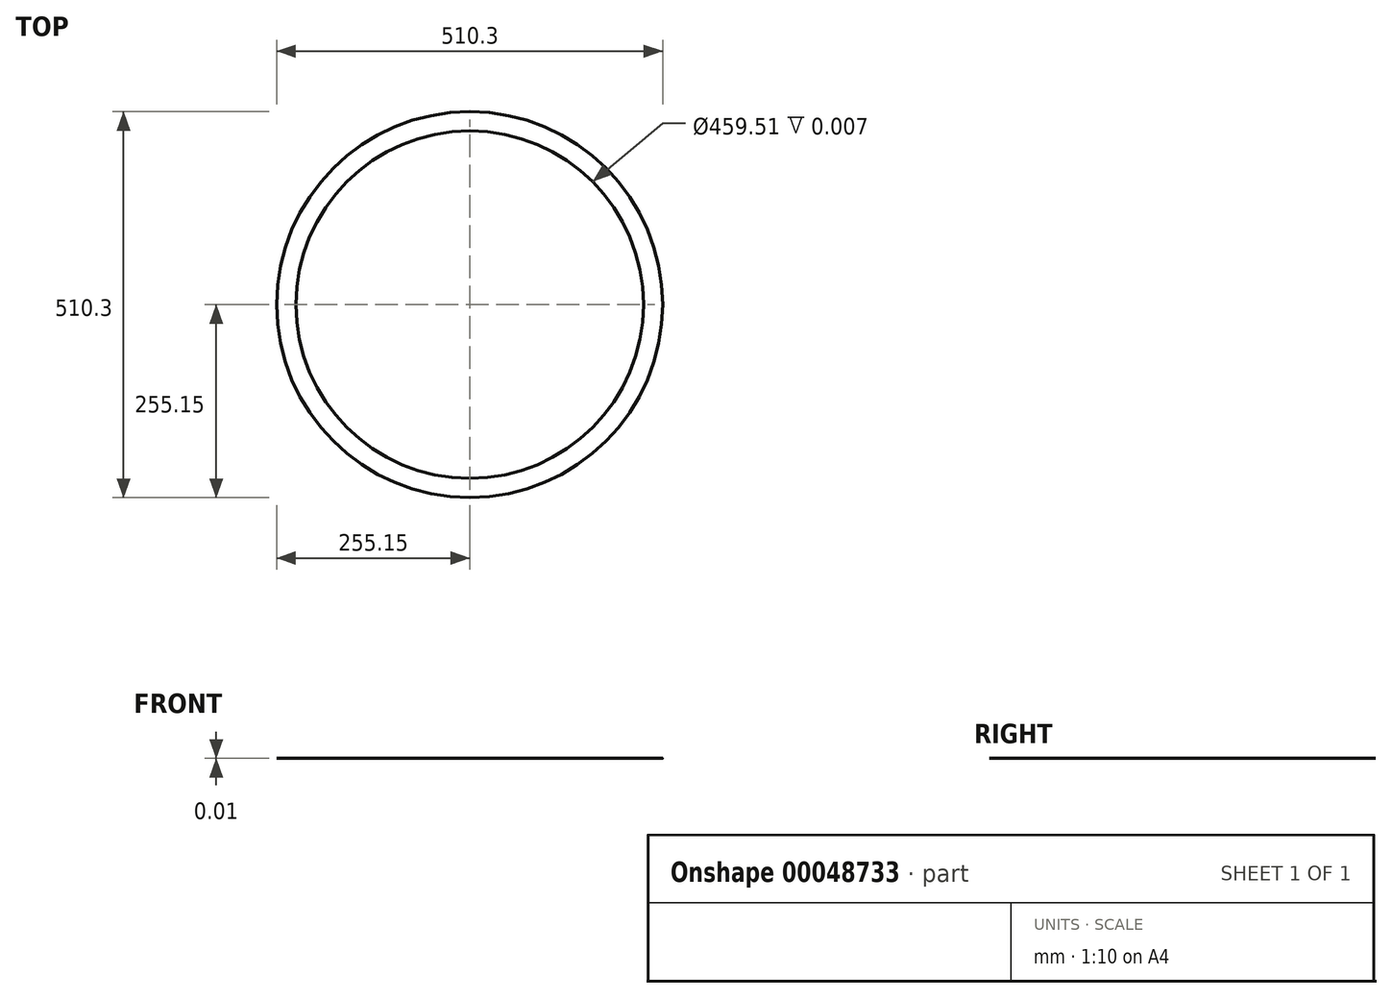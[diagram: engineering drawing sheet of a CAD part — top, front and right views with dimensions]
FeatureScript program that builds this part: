
annotation { "Feature Type Name" : "Feature", "Feature Type Description" : "" }
export const myFeature = defineFeature(function(context is Context, id is Id, definition is map)
    precondition{}
    {
        {
            var Q0;
            Q0=qCreatedBy(makeId("Top.planeOp"),FACE);
            var sketch = newSketch(context, id + "F0", { "sketchPlane" : qUnion([Q0])});
            skCircle(sketch, "E0", {"center": v(0, 0) * mm, "radius": 255.15 * mm});
            skCircle(sketch, "E1", {"center": v(0, 0) * mm, "radius": 229.75 * mm});
            skSolve(sketch);
        }
        {
            var Q0;
            Q0=makeQuery(id+"F0.imprint","IMPRINT",FACE,{"disambiguationData":[TD([[makeQuery(id+"F0.imprint","IMPRINT",EDGE,{"derivedFrom":sQuery(id+"F0.wireOp",EDGE,"E0")}),1.0]])]});
            extrude(context, id + "F1", {"entities" : qUnion([Q0]), "depth" : 3 / 406.4 * mm});
        }
    });
